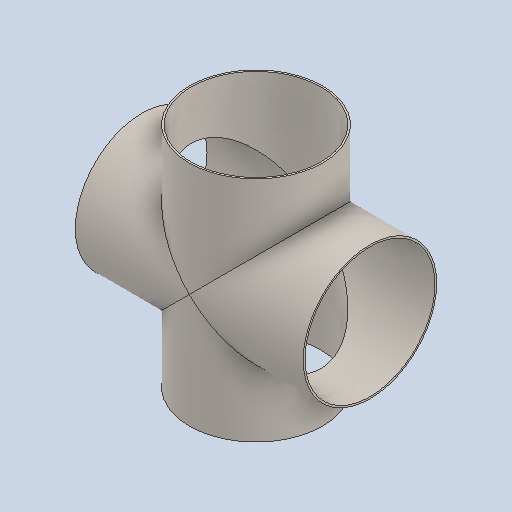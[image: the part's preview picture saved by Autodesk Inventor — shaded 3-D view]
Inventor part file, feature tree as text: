
AUTODESK INVENTOR PART (.ipt)
format: ipt  version: 2023 (Build 270158000, 158)  size: 157,184 bytes
history: native  units: in
note: dims shown in document units (in); Inventor stores cm internally (conversion verified against a paired STEP export)
features: shell x1
ambient origin geometry x8: Origin, YZ Plane, XZ Plane, XY Plane, X Axis, Y Axis, Z Axis, Center Point
bodies: Solid1 (feature_tree)
feature tree (1):
  shell  "Shell1"  [1 undecoded]
note: 1 required parameter value undecoded (feature->parameter linkage not recoverable at this tier; creation-order binding heuristic only, values carry confidence <= 0.55)
